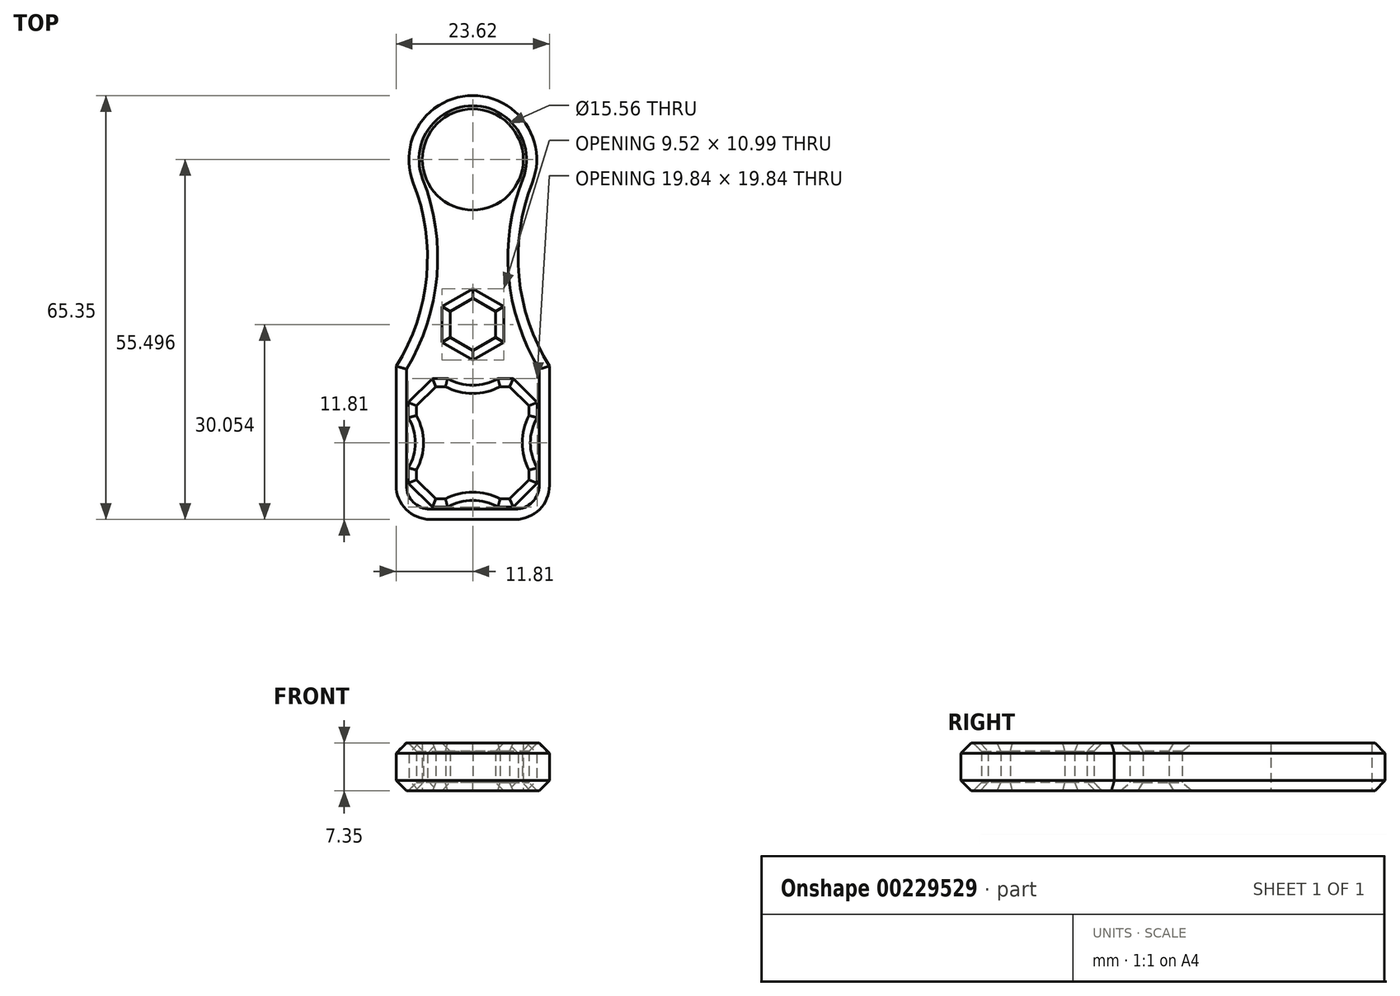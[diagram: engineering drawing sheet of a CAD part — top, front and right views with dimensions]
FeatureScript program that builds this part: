
annotation { "Feature Type Name" : "Feature", "Feature Type Description" : "" }
export const myFeature = defineFeature(function(context is Context, id is Id, definition is map)
    precondition{}
    {
        {
            var Q0;
            Q0=qCreatedBy(makeId("Top.planeOp"),FACE);
            var sketch = newSketch(context, id + "F0", { "sketchPlane" : qUnion([Q0])});
            skLineSegment(sketch, "E0.bottom", {"start": v(5.42, 8.25) * mm, "end": v(4, 8.25) * mm});
            skLineSegment(sketch, "E0.top", {"start": v(5.42, -8.25) * mm, "end": v(4, -8.25) * mm});
            skLineSegment(sketch, "E0.left", {"start": v(8.25, 5.42) * mm, "end": v(8.25, 4) * mm});
            skLineSegment(sketch, "E0.right", {"start": v(-8.25, 5.42) * mm, "end": v(-8.25, 4) * mm});
            skPoint(sketch, "E0.middle", {"position": v(0, 0) * mm});
            skArc(sketch, "E1", {"start": v(4, -8.25) * mm, "mid": v(0, -7.25) * mm, "end": v(-4, -8.25) * mm});
            skLineSegment(sketch, "E2", {"start": v(-8.25, -5.42) * mm, "end": v(-5.42, -8.25) * mm});
            skLineSegment(sketch, "E3.MirrorCS", {"start": v(8.25, -5.42) * mm, "end": v(5.42, -8.25) * mm});
            skLineSegment(sketch, "E4.MirrorCS", {"start": v(-8.25, 5.42) * mm, "end": v(-5.42, 8.25) * mm});
            skLineSegment(sketch, "E5.MirrorCS", {"start": v(8.25, 5.42) * mm, "end": v(5.42, 8.25) * mm});
            skArc(sketch, "E6", {"start": v(8.25, 4) * mm, "mid": v(7.25, 0) * mm, "end": v(8.25, -4) * mm});
            skArc(sketch, "E7.MirrorCS", {"start": v(-8.25, 4) * mm, "mid": v(-7.25, 0) * mm, "end": v(-8.25, -4) * mm});
            skArc(sketch, "E8.MirrorCS", {"start": v(4, 8.25) * mm, "mid": v(0, 7.25) * mm, "end": v(-4, 8.25) * mm});
            skPoint(sketch, "E9.orphan", {"position": v(-8.25, 8.25) * mm});
            skPoint(sketch, "E10.orphan", {"position": v(-8.25, -8.25) * mm});
            skLineSegment(sketch, "E11.trimOffspring", {"start": v(-8.25, -4) * mm, "end": v(-8.25, -5.42) * mm});
            skLineSegment(sketch, "E12.trimOffspring", {"start": v(-4, 8.25) * mm, "end": v(-5.42, 8.25) * mm});
            skPoint(sketch, "E13.orphan", {"position": v(8.25, 8.25) * mm});
            skLineSegment(sketch, "E14.trimOffspring", {"start": v(8.25, -4) * mm, "end": v(8.25, -5.42) * mm});
            skLineSegment(sketch, "E15.trimOffspring", {"start": v(-4, -8.25) * mm, "end": v(-5.42, -8.25) * mm});
            skPoint(sketch, "E16.orphan", {"position": v(8.25, -8.25) * mm});
            skLineSegment(sketch, "E17.bottom", {"start": v(11.25, 11.25) * mm, "end": v(-11.25, 11.25) * mm});
            skLineSegment(sketch, "E17.top", {"start": v(11.25, -11.25) * mm, "end": v(-11.25, -11.25) * mm});
            skLineSegment(sketch, "E17.left", {"start": v(11.25, 11.25) * mm, "end": v(11.25, -11.25) * mm});
            skLineSegment(sketch, "E17.right", {"start": v(-11.25, 11.25) * mm, "end": v(-11.25, -11.25) * mm});
            skArc(sketch, "E18", {"start": v(8.73, 38.18) * mm, "mid": v(6.79, 24.41) * mm, "end": v(11.25, 11.25) * mm});
            skArc(sketch, "E19.MirrorCS", {"start": v(-8.73, 38.18) * mm, "mid": v(-6.79, 24.41) * mm, "end": v(-11.25, 11.25) * mm});
            skCircle(sketch, "E20", {"center": v(0, 41.6) * mm, "radius": 9.38 * mm});
            skPoint(sketch, "E20.third.point", {"position": v(0, 50.99) * mm});
            skCircle(sketch, "E21", {"center": v(0, 41.6) * mm, "radius": 7.41 * mm});
            skCircle(sketch, "E22.cCircle", {"center": v(0, 17.38) * mm, "radius": 3.33 * mm, "construction": true});
            skLineSegment(sketch, "E22.0", {"start": v(0, 13.53) * mm, "end": v(-3.33, 15.45) * mm});
            skLineSegment(sketch, "E22.1", {"start": v(-3.33, 15.45) * mm, "end": v(-3.33, 19.3) * mm});
            skLineSegment(sketch, "E22.2", {"start": v(-3.33, 19.3) * mm, "end": v(0, 21.22) * mm});
            skLineSegment(sketch, "E22.3", {"start": v(0, 21.22) * mm, "end": v(3.33, 19.3) * mm});
            skLineSegment(sketch, "E22.4", {"start": v(3.33, 19.3) * mm, "end": v(3.33, 15.45) * mm});
            skLineSegment(sketch, "E22.5", {"start": v(3.33, 15.45) * mm, "end": v(0, 13.53) * mm});
            skPoint(sketch, "E22.0.midPoint", {"position": v(-1.67, 14.49) * mm});
            skSolve(sketch);
        }
        {
            var Q0;
            Q0=makeQuery(id+"F0.imprint","IMPRINT",FACE,{"disambiguationData":[TD([[makeQuery(id+"F0.imprint","IMPRINT",EDGE,{"derivedFrom":sQuery(id+"F0.wireOp",EDGE,"E0.bottom")}),-1.0]])]});
            var Q1;
            {var subQ0=sQuery(id+"F0.wireOp",EDGE,"E17.bottom");Q1=makeQuery(id+"F0.imprint","IMPRINT",FACE,{"disambiguationData":[TD([[makeQuery(id+"F0.imprint","IMPRINT",EDGE,{"derivedFrom":subQ0}),-1.0]])]});}
            var Q2;
            Q2=makeQuery(id+"F0.imprint","IMPRINT",FACE,{"disambiguationData":[TD([[makeQuery(id+"F0.imprint","IMPRINT",EDGE,{"derivedFrom":sQuery(id+"F0.wireOp",EDGE,"E21")}),-1.0]])]});
            extrude(context, id + "F1", {"entities" : qUnion([Q0, Q1, Q2]), "depth" : 7 * mm});
        }
        {
            var Q0;
            Q0=makeQuery(id+"F1.opExtrude","CAP_EDGE",EDGE,{"disambiguationData":[OSD([sQuery(id+"F0.wireOp",EDGE,"E7.MirrorCS")])],"isStart":false});
            var Q1;
            Q1=makeQuery(id+"F1.opExtrude","CAP_EDGE",EDGE,{"disambiguationData":[OSD([sQuery(id+"F0.wireOp",EDGE,"E0.right")])],"isStart":false});
            var Q2;
            Q2=makeQuery(id+"F1.opExtrude","CAP_EDGE",EDGE,{"disambiguationData":[OSD([sQuery(id+"F0.wireOp",EDGE,"E4.MirrorCS")])],"isStart":false});
            var Q3;
            Q3=makeQuery(id+"F1.opExtrude","CAP_EDGE",EDGE,{"disambiguationData":[OSD([sQuery(id+"F0.wireOp",EDGE,"E12.trimOffspring")])],"isStart":false});
            var Q4;
            Q4=makeQuery(id+"F1.opExtrude","CAP_EDGE",EDGE,{"disambiguationData":[OSD([sQuery(id+"F0.wireOp",EDGE,"E8.MirrorCS")])],"isStart":false});
            var Q5;
            Q5=makeQuery(id+"F1.opExtrude","CAP_EDGE",EDGE,{"disambiguationData":[OSD([sQuery(id+"F0.wireOp",EDGE,"E0.bottom")])],"isStart":false});
            var Q6;
            Q6=makeQuery(id+"F1.opExtrude","CAP_EDGE",EDGE,{"disambiguationData":[OSD([sQuery(id+"F0.wireOp",EDGE,"E5.MirrorCS")])],"isStart":false});
            var Q7;
            Q7=makeQuery(id+"F1.opExtrude","CAP_EDGE",EDGE,{"disambiguationData":[OSD([sQuery(id+"F0.wireOp",EDGE,"E0.left")])],"isStart":false});
            var Q8;
            Q8=makeQuery(id+"F1.opExtrude","CAP_EDGE",EDGE,{"disambiguationData":[OSD([sQuery(id+"F0.wireOp",EDGE,"E6")])],"isStart":false});
            var Q9;
            Q9=makeQuery(id+"F1.opExtrude","CAP_EDGE",EDGE,{"disambiguationData":[OSD([sQuery(id+"F0.wireOp",EDGE,"E14.trimOffspring")])],"isStart":false});
            var Q10;
            Q10=makeQuery(id+"F1.opExtrude","CAP_EDGE",EDGE,{"disambiguationData":[OSD([sQuery(id+"F0.wireOp",EDGE,"E3.MirrorCS")])],"isStart":false});
            var Q11;
            Q11=makeQuery(id+"F1.opExtrude","CAP_EDGE",EDGE,{"disambiguationData":[OSD([sQuery(id+"F0.wireOp",EDGE,"E0.top")])],"isStart":false});
            var Q12;
            Q12=makeQuery(id+"F1.opExtrude","CAP_EDGE",EDGE,{"disambiguationData":[OSD([sQuery(id+"F0.wireOp",EDGE,"E1")])],"isStart":false});
            var Q13;
            Q13=makeQuery(id+"F1.opExtrude","CAP_EDGE",EDGE,{"disambiguationData":[OSD([sQuery(id+"F0.wireOp",EDGE,"E15.trimOffspring")])],"isStart":false});
            var Q14;
            Q14=makeQuery(id+"F1.opExtrude","CAP_EDGE",EDGE,{"disambiguationData":[OSD([sQuery(id+"F0.wireOp",EDGE,"E2")])],"isStart":false});
            var Q15;
            Q15=makeQuery(id+"F1.opExtrude","CAP_EDGE",EDGE,{"disambiguationData":[OSD([sQuery(id+"F0.wireOp",EDGE,"E11.trimOffspring")])],"isStart":false});
            var Q16;
            Q16=makeQuery(id+"F1.opExtrude","CAP_EDGE",EDGE,{"disambiguationData":[OSD([sQuery(id+"F0.wireOp",EDGE,"E22.5")])],"isStart":false});
            var Q17;
            Q17=makeQuery(id+"F1.opExtrude","CAP_EDGE",EDGE,{"disambiguationData":[OSD([sQuery(id+"F0.wireOp",EDGE,"E22.0")])],"isStart":false});
            var Q18;
            Q18=makeQuery(id+"F1.opExtrude","CAP_EDGE",EDGE,{"disambiguationData":[OSD([sQuery(id+"F0.wireOp",EDGE,"E22.1")])],"isStart":false});
            var Q19;
            Q19=makeQuery(id+"F1.opExtrude","CAP_EDGE",EDGE,{"disambiguationData":[OSD([sQuery(id+"F0.wireOp",EDGE,"E22.2")])],"isStart":false});
            var Q20;
            Q20=makeQuery(id+"F1.opExtrude","CAP_EDGE",EDGE,{"disambiguationData":[OSD([sQuery(id+"F0.wireOp",EDGE,"E22.3")])],"isStart":false});
            var Q21;
            Q21=makeQuery(id+"F1.opExtrude","CAP_EDGE",EDGE,{"disambiguationData":[OSD([sQuery(id+"F0.wireOp",EDGE,"E22.4")])],"isStart":false});
            var Q22;
            Q22=makeQuery(id+"F1.opExtrude","CAP_EDGE",EDGE,{"disambiguationData":[OSD([sQuery(id+"F0.wireOp",EDGE,"E22.0")])],"isStart":true});
            var Q23;
            Q23=makeQuery(id+"F1.opExtrude","CAP_EDGE",EDGE,{"disambiguationData":[OSD([sQuery(id+"F0.wireOp",EDGE,"E22.5")])],"isStart":true});
            var Q24;
            Q24=makeQuery(id+"F1.opExtrude","CAP_EDGE",EDGE,{"disambiguationData":[OSD([sQuery(id+"F0.wireOp",EDGE,"E22.4")])],"isStart":true});
            var Q25;
            Q25=makeQuery(id+"F1.opExtrude","CAP_EDGE",EDGE,{"disambiguationData":[OSD([sQuery(id+"F0.wireOp",EDGE,"E22.3")])],"isStart":true});
            var Q26;
            Q26=makeQuery(id+"F1.opExtrude","CAP_EDGE",EDGE,{"disambiguationData":[OSD([sQuery(id+"F0.wireOp",EDGE,"E22.2")])],"isStart":true});
            var Q27;
            Q27=makeQuery(id+"F1.opExtrude","CAP_EDGE",EDGE,{"disambiguationData":[OSD([sQuery(id+"F0.wireOp",EDGE,"E1")])],"isStart":true});
            var Q28;
            Q28=makeQuery(id+"F1.opExtrude","CAP_EDGE",EDGE,{"disambiguationData":[OSD([sQuery(id+"F0.wireOp",EDGE,"E15.trimOffspring")])],"isStart":true});
            var Q29;
            Q29=makeQuery(id+"F1.opExtrude","CAP_EDGE",EDGE,{"disambiguationData":[OSD([sQuery(id+"F0.wireOp",EDGE,"E2")])],"isStart":true});
            var Q30;
            Q30=makeQuery(id+"F1.opExtrude","CAP_EDGE",EDGE,{"disambiguationData":[OSD([sQuery(id+"F0.wireOp",EDGE,"E11.trimOffspring")])],"isStart":true});
            var Q31;
            Q31=makeQuery(id+"F1.opExtrude","CAP_EDGE",EDGE,{"disambiguationData":[OSD([sQuery(id+"F0.wireOp",EDGE,"E7.MirrorCS")])],"isStart":true});
            var Q32;
            Q32=makeQuery(id+"F1.opExtrude","CAP_EDGE",EDGE,{"disambiguationData":[OSD([sQuery(id+"F0.wireOp",EDGE,"E0.right")])],"isStart":true});
            var Q33;
            Q33=makeQuery(id+"F1.opExtrude","CAP_EDGE",EDGE,{"disambiguationData":[OSD([sQuery(id+"F0.wireOp",EDGE,"E12.trimOffspring")])],"isStart":true});
            var Q34;
            Q34=makeQuery(id+"F1.opExtrude","CAP_EDGE",EDGE,{"disambiguationData":[OSD([sQuery(id+"F0.wireOp",EDGE,"E0.bottom")])],"isStart":true});
            var Q35;
            Q35=makeQuery(id+"F1.opExtrude","CAP_EDGE",EDGE,{"disambiguationData":[OSD([sQuery(id+"F0.wireOp",EDGE,"E4.MirrorCS")])],"isStart":true});
            var Q36;
            Q36=makeQuery(id+"F1.opExtrude","CAP_EDGE",EDGE,{"disambiguationData":[OSD([sQuery(id+"F0.wireOp",EDGE,"E8.MirrorCS")])],"isStart":true});
            var Q37;
            Q37=makeQuery(id+"F1.opExtrude","CAP_EDGE",EDGE,{"disambiguationData":[OSD([sQuery(id+"F0.wireOp",EDGE,"E5.MirrorCS")])],"isStart":true});
            var Q38;
            Q38=makeQuery(id+"F1.opExtrude","CAP_EDGE",EDGE,{"disambiguationData":[OSD([sQuery(id+"F0.wireOp",EDGE,"E0.left")])],"isStart":true});
            var Q39;
            Q39=makeQuery(id+"F1.opExtrude","CAP_EDGE",EDGE,{"disambiguationData":[OSD([sQuery(id+"F0.wireOp",EDGE,"E6")])],"isStart":true});
            var Q40;
            Q40=makeQuery(id+"F1.opExtrude","CAP_EDGE",EDGE,{"disambiguationData":[OSD([sQuery(id+"F0.wireOp",EDGE,"E14.trimOffspring")])],"isStart":true});
            var Q41;
            Q41=makeQuery(id+"F1.opExtrude","CAP_EDGE",EDGE,{"disambiguationData":[OSD([sQuery(id+"F0.wireOp",EDGE,"E3.MirrorCS")])],"isStart":true});
            var Q42;
            Q42=makeQuery(id+"F1.opExtrude","CAP_EDGE",EDGE,{"disambiguationData":[OSD([sQuery(id+"F0.wireOp",EDGE,"E0.top")])],"isStart":true});
            var Q43;
            Q43=makeQuery(id+"F1.opExtrude","CAP_EDGE",EDGE,{"disambiguationData":[OSD([sQuery(id+"F0.wireOp",EDGE,"E22.1")])],"isStart":true});
            chamfer(context, id + "F2", {"entities" : qUnion([Q0, Q1, Q2, Q3, Q4, Q5, Q6, Q7, Q8, Q9, Q10, Q11, Q12, Q13, Q14, Q15, Q16, Q17, Q18, Q19, Q20, Q21, Q22, Q23, Q24, Q25, Q26, Q27, Q28, Q29, Q30, Q31, Q32, Q33, Q34, Q35, Q36, Q37, Q38, Q39, Q40, Q41, Q42, Q43]), "width" : 1.2 * mm, "tangentPropagation" : true});
        }
        {
            var Q0;
            Q0=makeQuery(id+"F1.opExtrude","SWEPT_EDGE",EDGE,{"disambiguationData":[OSD([sQuery(id+"F0.wireOp",EDGE,"E17.top"),sQuery(id+"F0.wireOp",EDGE,"E17.left")])]});
            var Q1;
            Q1=makeQuery(id+"F1.opExtrude","SWEPT_EDGE",EDGE,{"disambiguationData":[OSD([sQuery(id+"F0.wireOp",EDGE,"E17.top"),sQuery(id+"F0.wireOp",EDGE,"E17.right")])]});
            fillet(context, id + "F3", {"entities" : qUnion([Q0, Q1]), "radius" : 5 * mm, "tangentPropagation" : true, "allowEdgeOverflow" : false});
        }
        {
            var Q0;
            Q0=makeQuery(id+"F1.opExtrude","CAP_EDGE",EDGE,{"disambiguationData":[OSD([sQuery(id+"F0.wireOp",EDGE,"E20")])],"isStart":false});
            var Q1;
            Q1=makeQuery(id+"F1.opExtrude","CAP_EDGE",EDGE,{"disambiguationData":[OSD([sQuery(id+"F0.wireOp",EDGE,"E17.left")])],"isStart":false});
            var Q2;
            Q2=makeQuery(id+"F1.opExtrude","CAP_EDGE",EDGE,{"disambiguationData":[OSD([sQuery(id+"F0.wireOp",EDGE,"E17.top")])],"isStart":false});
            var Q3;
            Q3=makeQuery(id+"F1.opExtrude","CAP_EDGE",EDGE,{"disambiguationData":[OSD([sQuery(id+"F0.wireOp",EDGE,"E17.right")])],"isStart":false});
            var Q4;
            Q4=makeQuery(id+"F1.opExtrude","CAP_EDGE",EDGE,{"disambiguationData":[OSD([sQuery(id+"F0.wireOp",EDGE,"E20")])],"isStart":true});
            var Q5;
            Q5=makeQuery(id+"F1.opExtrude","CAP_EDGE",EDGE,{"disambiguationData":[OSD([sQuery(id+"F0.wireOp",EDGE,"E17.right")])],"isStart":true});
            var Q6;
            Q6=makeQuery(id+"F1.opExtrude","CAP_EDGE",EDGE,{"disambiguationData":[OSD([sQuery(id+"F0.wireOp",EDGE,"E17.top")])],"isStart":true});
            var Q7;
            Q7=makeQuery(id+"F1.opExtrude","CAP_EDGE",EDGE,{"disambiguationData":[OSD([sQuery(id+"F0.wireOp",EDGE,"E17.left")])],"isStart":true});
            chamfer(context, id + "F4", {"entities" : qUnion([Q0, Q1, Q2, Q3, Q4, Q5, Q6, Q7]), "width" : 1.5 * mm, "tangentPropagation" : true});
        }
        {
            var Q0;
            Q0=makeQuery(id+"F1.opExtrude","SWEPT_BODY",BODY,{"disambiguationData":[OSD([sQuery(id+"F0.wireOp",EDGE,"E0.bottom"),sQuery(id+"F0.wireOp",EDGE,"E0.top"),sQuery(id+"F0.wireOp",EDGE,"E0.left"),sQuery(id+"F0.wireOp",EDGE,"E0.right"),sQuery(id+"F0.wireOp",EDGE,"E1"),sQuery(id+"F0.wireOp",EDGE,"E2"),sQuery(id+"F0.wireOp",EDGE,"E3.MirrorCS"),sQuery(id+"F0.wireOp",EDGE,"E4.MirrorCS"),sQuery(id+"F0.wireOp",EDGE,"E5.MirrorCS"),sQuery(id+"F0.wireOp",EDGE,"E6"),sQuery(id+"F0.wireOp",EDGE,"E7.MirrorCS"),sQuery(id+"F0.wireOp",EDGE,"E8.MirrorCS"),sQuery(id+"F0.wireOp",EDGE,"E11.trimOffspring"),sQuery(id+"F0.wireOp",EDGE,"E12.trimOffspring"),sQuery(id+"F0.wireOp",EDGE,"E14.trimOffspring"),sQuery(id+"F0.wireOp",EDGE,"E15.trimOffspring"),sQuery(id+"F0.wireOp",EDGE,"E17.bottom"),sQuery(id+"F0.wireOp",EDGE,"E17.top"),sQuery(id+"F0.wireOp",EDGE,"E17.left"),sQuery(id+"F0.wireOp",EDGE,"E17.right")])]});
            var Q1;
            Q1=qCreatedBy(makeId("Origin.pointOp"),VERTEX);
            transform(context, id + "F5", {"entities" : qUnion([Q0]), "transformType" : TransformType.SCALE_UNIFORMLY, "scale" : 1.05, "scalePoint" : qUnion([Q1]), "makeCopy" : false});
        }
    });
